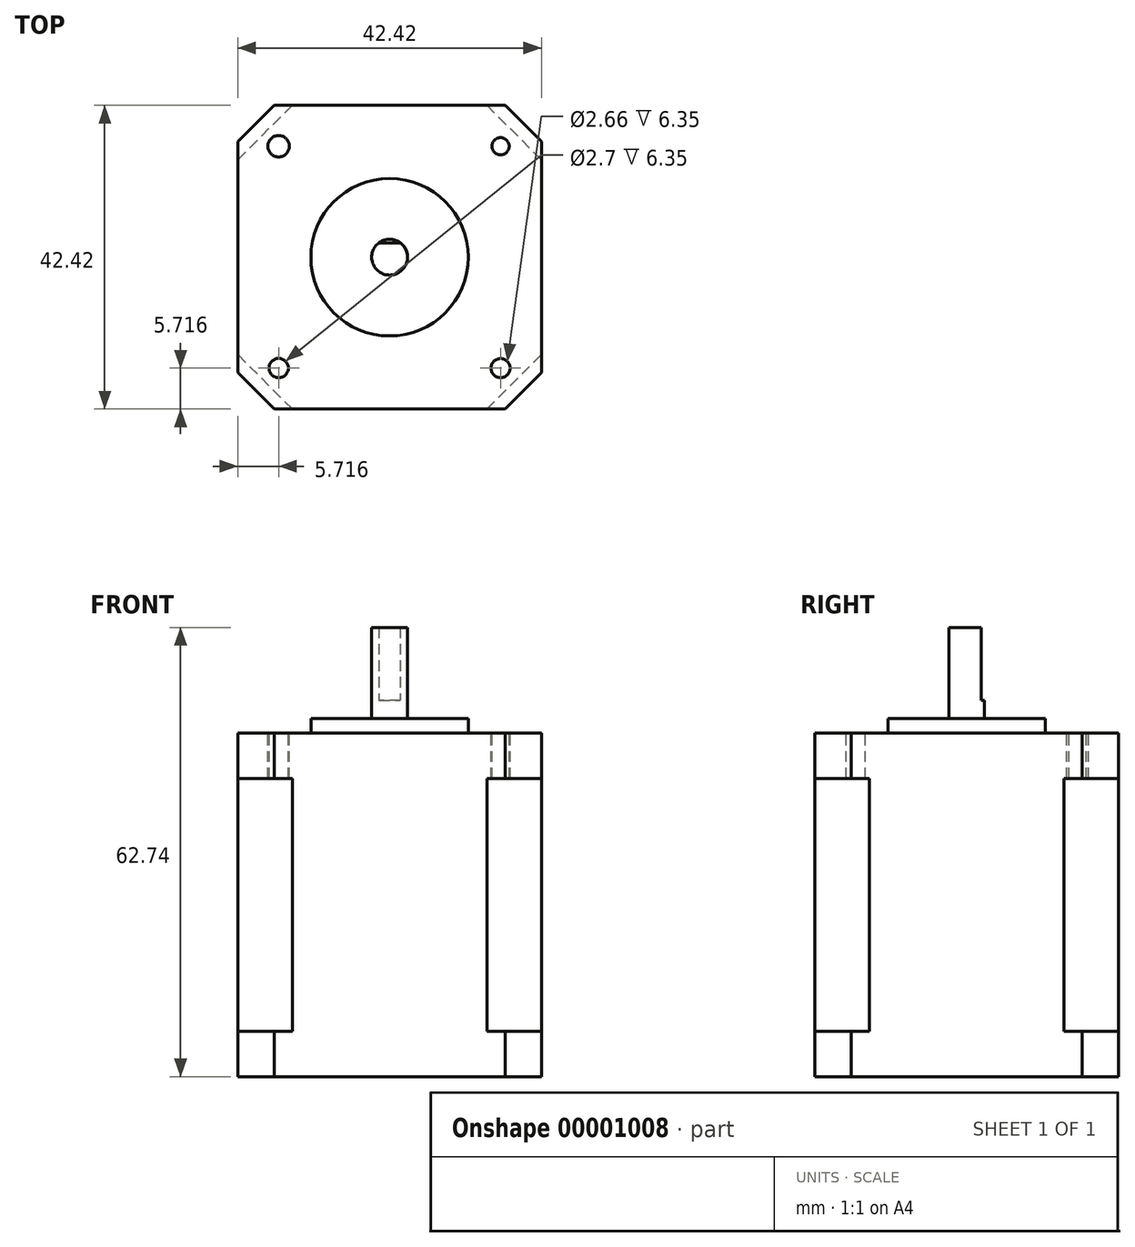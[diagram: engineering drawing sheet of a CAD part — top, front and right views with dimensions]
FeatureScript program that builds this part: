
annotation { "Feature Type Name" : "Feature", "Feature Type Description" : "" }
export const myFeature = defineFeature(function(context is Context, id is Id, definition is map)
    precondition{}
    {
        {
            var Q0;
            Q0=qCreatedBy(makeId("Top.planeOp"),FACE);
            var sketch = newSketch(context, id + "F0", { "sketchPlane" : qUnion([Q0])});
            skLineSegment(sketch, "E0.bottom", {"start": v(-21.2, 21.2) * mm, "end": v(21.2, 21.2) * mm});
            skLineSegment(sketch, "E0.top", {"start": v(-21.2, -21.2) * mm, "end": v(21.2, -21.2) * mm});
            skLineSegment(sketch, "E0.left", {"start": v(-21.2, 21.2) * mm, "end": v(-21.2, -21.2) * mm});
            skLineSegment(sketch, "E0.right", {"start": v(21.2, 21.2) * mm, "end": v(21.2, -21.2) * mm});
            skSolve(sketch);
        }
        {
            var Q0;
            Q0=makeQuery(id+"F0.imprint","IMPRINT",FACE,{"disambiguationData":[TD([[makeQuery(id+"F0.imprint","IMPRINT",EDGE,{"derivedFrom":sQuery(id+"F0.wireOp",EDGE,"E0.bottom")}),-1.0]])]});
            extrude(context, id + "F1", {"entities" : qUnion([Q0]), "endBound" : BoundingType.SYMMETRIC, "depth" : 35.3 * mm});
        }
        {
            var Q0;
            Q0=makeQuery(id+"F1.opExtrude","SWEPT_EDGE",EDGE,{"disambiguationData":[OSD([sQuery(id+"F0.wireOp",EDGE,"E0.bottom"),sQuery(id+"F0.wireOp",EDGE,"E0.right")])]});
            var Q1;
            Q1=makeQuery(id+"F1.opExtrude","SWEPT_EDGE",EDGE,{"disambiguationData":[OSD([sQuery(id+"F0.wireOp",EDGE,"E0.bottom"),sQuery(id+"F0.wireOp",EDGE,"E0.left")])]});
            var Q2;
            Q2=makeQuery(id+"F1.opExtrude","SWEPT_EDGE",EDGE,{"disambiguationData":[OSD([sQuery(id+"F0.wireOp",EDGE,"E0.top"),sQuery(id+"F0.wireOp",EDGE,"E0.left")])]});
            var Q3;
            Q3=makeQuery(id+"F1.opExtrude","SWEPT_EDGE",EDGE,{"disambiguationData":[OSD([sQuery(id+"F0.wireOp",EDGE,"E0.top"),sQuery(id+"F0.wireOp",EDGE,"E0.right")])]});
            chamfer(context, id + "F2", {"entities" : qUnion([Q0, Q1, Q2, Q3]), "width" : 7.62 * mm, "tangentPropagation" : true});
        }
        {
            var Q0;
            Q0=makeQuery(id+"F1.opExtrude","CAP_FACE",FACE,{"disambiguationData":[OSD([sQuery(id+"F0.wireOp",EDGE,"E0.bottom"),sQuery(id+"F0.wireOp",EDGE,"E0.top"),sQuery(id+"F0.wireOp",EDGE,"E0.left"),sQuery(id+"F0.wireOp",EDGE,"E0.right")])],"isStart":false});
            var sketch = newSketch(context, id + "F3", { "sketchPlane" : qUnion([Q0])});
            skLineSegment(sketch, "E1.bottom", {"start": v(-21.2, 21.2) * mm, "end": v(21.2, 21.2) * mm});
            skLineSegment(sketch, "E1.top", {"start": v(-21.2, -21.2) * mm, "end": v(21.2, -21.2) * mm});
            skLineSegment(sketch, "E1.left", {"start": v(-21.2, 21.2) * mm, "end": v(-21.2, -21.2) * mm});
            skLineSegment(sketch, "E1.right", {"start": v(21.2, 21.2) * mm, "end": v(21.2, -21.2) * mm});
            skSolve(sketch);
        }
        {
            var Q0;
            {var subQ0=sQuery(id+"F0.wireOp",EDGE,"E0.top");var subQ1=sQuery(id+"F0.wireOp",EDGE,"E0.right");var subQ2=sQuery(id+"F0.wireOp",EDGE,"E0.bottom");var subQ3=sQuery(id+"F0.wireOp",EDGE,"E0.left");var subQ4=makeQuery(id+"F1.opExtrude","CAP_FACE",FACE,{"disambiguationData":[OSD([subQ2,subQ0,subQ3,subQ1])],"isStart":false});var subQ8=makeQuery(id+"F2.opChamfer","BLEND_EDGE",EDGE,{"blendedFrom":[makeQuery(id+"F1.opExtrude","SWEPT_EDGE",EDGE,{"disambiguationData":[OSD([subQ2,subQ3])]}),subQ4],"blendedInto":[subQ4]});Q0=makeQuery(id+"F3.imprint","IMPRINT",FACE,{"disambiguationData":[TD([[makeQuery(id+"F3.imprint","IMPRINT",EDGE,{"derivedFrom":subQ8}),1.0]])]});}
            var Q1;
            {var subQ0=sQuery(id+"F0.wireOp",EDGE,"E0.bottom");var subQ1=sQuery(id+"F0.wireOp",EDGE,"E0.right");var subQ2=makeQuery(id+"F2.opChamfer","BLEND_EDGE",EDGE,{"blendedFrom":[makeQuery(id+"F1.opExtrude","SWEPT_EDGE",EDGE,{"disambiguationData":[OSD([subQ0,subQ1])]}),makeQuery(id+"F1.opExtrude","CAP_FACE",FACE,{"disambiguationData":[OSD([subQ0,sQuery(id+"F0.wireOp",EDGE,"E0.top"),sQuery(id+"F0.wireOp",EDGE,"E0.left"),subQ1])],"isStart":false})],"blendedInto":[makeQuery(id+"F1.opExtrude","CAP_FACE",FACE,{"disambiguationData":[OSD([subQ0,sQuery(id+"F0.wireOp",EDGE,"E0.top"),sQuery(id+"F0.wireOp",EDGE,"E0.left"),subQ1])],"isStart":false})]});Q1=makeQuery(id+"F3.imprint","IMPRINT",FACE,{"disambiguationData":[TD([[makeQuery(id+"F3.imprint","IMPRINT",EDGE,{"derivedFrom":subQ2}),-1.0]])]});}
            var Q2;
            {var subQ0=sQuery(id+"F0.wireOp",EDGE,"E0.bottom");var subQ1=sQuery(id+"F0.wireOp",EDGE,"E0.left");var subQ2=makeQuery(id+"F2.opChamfer","BLEND_EDGE",EDGE,{"blendedFrom":[makeQuery(id+"F1.opExtrude","SWEPT_EDGE",EDGE,{"disambiguationData":[OSD([subQ0,subQ1])]}),makeQuery(id+"F1.opExtrude","CAP_FACE",FACE,{"disambiguationData":[OSD([subQ0,sQuery(id+"F0.wireOp",EDGE,"E0.top"),subQ1,sQuery(id+"F0.wireOp",EDGE,"E0.right")])],"isStart":false})],"blendedInto":[makeQuery(id+"F1.opExtrude","CAP_FACE",FACE,{"disambiguationData":[OSD([subQ0,sQuery(id+"F0.wireOp",EDGE,"E0.top"),subQ1,sQuery(id+"F0.wireOp",EDGE,"E0.right")])],"isStart":false})]});Q2=makeQuery(id+"F3.imprint","IMPRINT",FACE,{"disambiguationData":[TD([[makeQuery(id+"F3.imprint","IMPRINT",EDGE,{"derivedFrom":subQ2}),-1.0]])]});}
            var Q3;
            {var subQ0=sQuery(id+"F0.wireOp",EDGE,"E0.top");var subQ1=sQuery(id+"F0.wireOp",EDGE,"E0.left");var subQ2=makeQuery(id+"F2.opChamfer","BLEND_EDGE",EDGE,{"blendedFrom":[makeQuery(id+"F1.opExtrude","SWEPT_EDGE",EDGE,{"disambiguationData":[OSD([subQ0,subQ1])]}),makeQuery(id+"F1.opExtrude","CAP_FACE",FACE,{"disambiguationData":[OSD([sQuery(id+"F0.wireOp",EDGE,"E0.bottom"),subQ0,subQ1,sQuery(id+"F0.wireOp",EDGE,"E0.right")])],"isStart":false})],"blendedInto":[makeQuery(id+"F1.opExtrude","CAP_FACE",FACE,{"disambiguationData":[OSD([sQuery(id+"F0.wireOp",EDGE,"E0.bottom"),subQ0,subQ1,sQuery(id+"F0.wireOp",EDGE,"E0.right")])],"isStart":false})]});Q3=makeQuery(id+"F3.imprint","IMPRINT",FACE,{"disambiguationData":[TD([[makeQuery(id+"F3.imprint","IMPRINT",EDGE,{"derivedFrom":subQ2}),-1.0]])]});}
            var Q4;
            {var subQ0=sQuery(id+"F0.wireOp",EDGE,"E0.top");var subQ1=sQuery(id+"F0.wireOp",EDGE,"E0.right");var subQ2=makeQuery(id+"F2.opChamfer","BLEND_EDGE",EDGE,{"blendedFrom":[makeQuery(id+"F1.opExtrude","SWEPT_EDGE",EDGE,{"disambiguationData":[OSD([subQ0,subQ1])]}),makeQuery(id+"F1.opExtrude","CAP_FACE",FACE,{"disambiguationData":[OSD([sQuery(id+"F0.wireOp",EDGE,"E0.bottom"),subQ0,sQuery(id+"F0.wireOp",EDGE,"E0.left"),subQ1])],"isStart":false})],"blendedInto":[makeQuery(id+"F1.opExtrude","CAP_FACE",FACE,{"disambiguationData":[OSD([sQuery(id+"F0.wireOp",EDGE,"E0.bottom"),subQ0,sQuery(id+"F0.wireOp",EDGE,"E0.left"),subQ1])],"isStart":false})]});Q4=makeQuery(id+"F3.imprint","IMPRINT",FACE,{"disambiguationData":[TD([[makeQuery(id+"F3.imprint","IMPRINT",EDGE,{"derivedFrom":subQ2}),-1.0]])]});}
            extrude(context, id + "F4", {"entities" : qUnion([Q0, Q1, Q2, Q3, Q4]), "operationType" : NewBodyOperationType.ADD, "depth" : 6.35 * mm});
        }
        {
            var Q0;
            Q0=makeQuery(id+"F4.opExtrude","SWEPT_EDGE",EDGE,{"disambiguationData":[OSD([sQuery(id+"F3.wireOp",EDGE,"E1.bottom"),sQuery(id+"F3.wireOp",EDGE,"E1.right")])]});
            var Q1;
            Q1=makeQuery(id+"F4.opExtrude","SWEPT_EDGE",EDGE,{"disambiguationData":[OSD([sQuery(id+"F3.wireOp",EDGE,"E1.bottom"),sQuery(id+"F3.wireOp",EDGE,"E1.left")])]});
            var Q2;
            Q2=makeQuery(id+"F4.opExtrude","SWEPT_EDGE",EDGE,{"disambiguationData":[OSD([sQuery(id+"F3.wireOp",EDGE,"E1.top"),sQuery(id+"F3.wireOp",EDGE,"E1.left")])]});
            var Q3;
            Q3=makeQuery(id+"F4.opExtrude","SWEPT_EDGE",EDGE,{"disambiguationData":[OSD([sQuery(id+"F3.wireOp",EDGE,"E1.top"),sQuery(id+"F3.wireOp",EDGE,"E1.right")])]});
            chamfer(context, id + "F5", {"entities" : qUnion([Q0, Q1, Q2, Q3]), "width" : 5.08 * mm, "tangentPropagation" : true});
        }
        {
            var Q0;
            Q0=makeQuery(id+"F1.opExtrude","CAP_FACE",FACE,{"disambiguationData":[OSD([sQuery(id+"F0.wireOp",EDGE,"E0.bottom"),sQuery(id+"F0.wireOp",EDGE,"E0.top"),sQuery(id+"F0.wireOp",EDGE,"E0.left"),sQuery(id+"F0.wireOp",EDGE,"E0.right")])],"isStart":true});
            var sketch = newSketch(context, id + "F6", { "sketchPlane" : qUnion([Q0])});
            skLineSegment(sketch, "E2.0.0", {"start": v(-16.13, 21.2) * mm, "end": v(16.13, 21.2) * mm});
            skLineSegment(sketch, "E2.0.1", {"start": v(16.13, 21.2) * mm, "end": v(21.2, 16.13) * mm});
            skLineSegment(sketch, "E2.0.2", {"start": v(21.2, -16.13) * mm, "end": v(21.2, 16.13) * mm});
            skLineSegment(sketch, "E2.0.3", {"start": v(21.2, -16.13) * mm, "end": v(16.13, -21.2) * mm});
            skLineSegment(sketch, "E2.0.4", {"start": v(-16.13, -21.2) * mm, "end": v(16.13, -21.2) * mm});
            skLineSegment(sketch, "E2.0.5", {"start": v(-16.13, -21.2) * mm, "end": v(-21.2, -16.13) * mm});
            skLineSegment(sketch, "E2.0.6", {"start": v(-21.2, -16.13) * mm, "end": v(-21.2, 16.13) * mm});
            skLineSegment(sketch, "E2.0.7", {"start": v(-21.2, 16.13) * mm, "end": v(-16.13, 21.2) * mm});
            skSolve(sketch);
        }
        {
            var Q0;
            {var subQ3=sQuery(id+"F6.wireOp",EDGE,"E2.0.7");Q0=makeQuery(id+"F6.imprint","IMPRINT",FACE,{"disambiguationData":[TD([[makeQuery(id+"F6.imprint","IMPRINT",EDGE,{"derivedFrom":subQ3}),-1.0]])]});}
            var Q1;
            {var subQ4=sQuery(id+"F6.wireOp",EDGE,"E2.0.1");Q1=makeQuery(id+"F6.imprint","IMPRINT",FACE,{"disambiguationData":[TD([[makeQuery(id+"F6.imprint","IMPRINT",EDGE,{"derivedFrom":subQ4}),-1.0]])]});}
            var Q2;
            {var subQ4=sQuery(id+"F6.wireOp",EDGE,"E2.0.3");Q2=makeQuery(id+"F6.imprint","IMPRINT",FACE,{"disambiguationData":[TD([[makeQuery(id+"F6.imprint","IMPRINT",EDGE,{"derivedFrom":subQ4}),-1.0]])]});}
            var Q3;
            {var subQ4=sQuery(id+"F6.wireOp",EDGE,"E2.0.5");Q3=makeQuery(id+"F6.imprint","IMPRINT",FACE,{"disambiguationData":[TD([[makeQuery(id+"F6.imprint","IMPRINT",EDGE,{"derivedFrom":subQ4}),-1.0]])]});}
            var Q4;
            {var subQ0=sQuery(id+"F0.wireOp",EDGE,"E0.top");var subQ1=sQuery(id+"F0.wireOp",EDGE,"E0.right");var subQ2=sQuery(id+"F0.wireOp",EDGE,"E0.bottom");var subQ3=sQuery(id+"F0.wireOp",EDGE,"E0.left");var subQ4=makeQuery(id+"F1.opExtrude","CAP_FACE",FACE,{"disambiguationData":[OSD([subQ2,subQ0,subQ3,subQ1])],"isStart":true});var subQ8=makeQuery(id+"F2.opChamfer","BLEND_EDGE",EDGE,{"blendedFrom":[makeQuery(id+"F1.opExtrude","SWEPT_EDGE",EDGE,{"disambiguationData":[OSD([subQ2,subQ3])]}),subQ4],"blendedInto":[subQ4]});Q4=makeQuery(id+"F6.imprint","IMPRINT",FACE,{"disambiguationData":[TD([[makeQuery(id+"F6.imprint","IMPRINT",EDGE,{"derivedFrom":subQ8}),1.0]])]});}
            extrude(context, id + "F7", {"entities" : qUnion([Q0, Q1, Q2, Q3, Q4]), "operationType" : NewBodyOperationType.ADD, "depth" : 6.35 * mm});
        }
        {
            var Q0;
            Q0=makeQuery(id+"F4.opExtrude","CAP_FACE",FACE,{"disambiguationData":[OSD([sQuery(id+"F3.wireOp",EDGE,"E1.bottom"),sQuery(id+"F3.wireOp",EDGE,"E1.top"),sQuery(id+"F3.wireOp",EDGE,"E1.left"),sQuery(id+"F3.wireOp",EDGE,"E1.right")])],"isStart":false});
            var sketch = newSketch(context, id + "F8", { "sketchPlane" : qUnion([Q0])});
            skCircle(sketch, "E3", {"center": v(0, 0) * mm, "radius": 11 * mm});
            skSolve(sketch);
        }
        {
            var Q0;
            Q0=makeQuery(id+"F8.imprint","IMPRINT",FACE,{"disambiguationData":[TD([[makeQuery(id+"F8.imprint","IMPRINT",EDGE,{"derivedFrom":sQuery(id+"F8.wireOp",EDGE,"E3")}),1.0]])]});
            extrude(context, id + "F9", {"entities" : qUnion([Q0]), "operationType" : NewBodyOperationType.ADD, "depth" : 2.03 * mm});
        }
        {
            var Q0;
            Q0=makeQuery(id+"F9.opExtrude","CAP_FACE",FACE,{"disambiguationData":[OSD([sQuery(id+"F8.wireOp",EDGE,"E3")])],"isStart":false});
            var sketch = newSketch(context, id + "F10", { "sketchPlane" : qUnion([Q0])});
            skCircle(sketch, "E4", {"center": v(0, 0) * mm, "radius": 2.5 * mm});
            skSolve(sketch);
        }
        {
            var Q0;
            Q0=makeQuery(id+"F10.imprint","IMPRINT",FACE,{"disambiguationData":[TD([[makeQuery(id+"F10.imprint","IMPRINT",EDGE,{"derivedFrom":sQuery(id+"F10.wireOp",EDGE,"E4")}),1.0]])]});
            extrude(context, id + "F11", {"entities" : qUnion([Q0]), "operationType" : NewBodyOperationType.ADD, "depth" : 12.7 * mm});
        }
        {
            var Q0;
            Q0=makeQuery(id+"F11.opExtrude","CAP_FACE",FACE,{"disambiguationData":[OSD([sQuery(id+"F10.wireOp",EDGE,"E4")])],"isStart":false});
            var sketch = newSketch(context, id + "F12", { "sketchPlane" : qUnion([Q0])});
            skLineSegment(sketch, "E5.bottom", {"start": v(-2.63, 2.93) * mm, "end": v(2.62, 2.93) * mm});
            skLineSegment(sketch, "E5.top", {"start": v(-2.63, 2) * mm, "end": v(2.62, 2) * mm});
            skLineSegment(sketch, "E5.left", {"start": v(-2.63, 2.93) * mm, "end": v(-2.63, 2) * mm});
            skLineSegment(sketch, "E5.right", {"start": v(2.62, 2.93) * mm, "end": v(2.62, 2) * mm});
            skSolve(sketch);
        }
        {
            var Q0;
            {var subQ0=makeQuery(id+"F11.opExtrude","CAP_EDGE",EDGE,{"disambiguationData":[OSD([sQuery(id+"F10.wireOp",EDGE,"E4")])],"isStart":false});var subQ1=sQuery(id+"F12.wireOp",EDGE,"E5.top");var subQ3=makeQuery(id+"F12.imprint","INTERSECT",VERTEX,{"disambiguationData":[OD(0.0)],"derivedFrom":[subQ0,subQ1]});Q0=qUnion([makeQuery(id+"F12.imprint","IMPRINT",FACE,{"disambiguationData":[TD([[makeQuery(id+"F12.imprint","IMPRINT",EDGE,{"derivedFrom":sQuery(id+"F12.wireOp",EDGE,"E5.bottom")}),-1.0]])]}),makeQuery(id+"F12.imprint","IMPRINT",FACE,{"disambiguationData":[TD([[makeQuery(id+"F12.imprint","IMPRINT",EDGE,{"disambiguationData":[TD([[subQ3,-1.0]])],"derivedFrom":subQ1}),1.0]])]})]);}
            extrude(context, id + "F13", {"entities" : qUnion([Q0]), "operationType" : NewBodyOperationType.REMOVE, "oppositeDirection" : true, "depth" : 10.16 * mm});
        }
        {
            var Q0;
            Q0=makeQuery(id+"F4.opExtrude","CAP_FACE",FACE,{"disambiguationData":[OSD([sQuery(id+"F3.wireOp",EDGE,"E1.bottom"),sQuery(id+"F3.wireOp",EDGE,"E1.top"),sQuery(id+"F3.wireOp",EDGE,"E1.left"),sQuery(id+"F3.wireOp",EDGE,"E1.right")])],"isStart":false});
            var sketch = newSketch(context, id + "F14", { "sketchPlane" : qUnion([Q0])});
            skCircle(sketch, "E6", {"center": v(-15.5, 15.5) * mm, "radius": 1.5 * mm});
            skCircle(sketch, "E7", {"center": v(15.5, 15.5) * mm, "radius": 1.2 * mm});
            skCircle(sketch, "E8", {"center": v(15.5, -15.5) * mm, "radius": 1.33 * mm});
            skCircle(sketch, "E9", {"center": v(-15.5, -15.5) * mm, "radius": 1.35 * mm});
            skSolve(sketch);
        }
        {
            var Q0;
            {Q0=qUnion([makeQuery(id+"F14.imprint","IMPRINT",FACE,{"disambiguationData":[TD([[makeQuery(id+"F14.imprint","IMPRINT",EDGE,{"derivedFrom":sQuery(id+"F14.wireOp",EDGE,"E6")}),1.0]])]}),makeQuery(id+"F14.imprint","IMPRINT",FACE,{"disambiguationData":[TD([[makeQuery(id+"F14.imprint","IMPRINT",EDGE,{"derivedFrom":sQuery(id+"F14.wireOp",EDGE,"E7")}),1.0]])]}),makeQuery(id+"F14.imprint","IMPRINT",FACE,{"disambiguationData":[TD([[makeQuery(id+"F14.imprint","IMPRINT",EDGE,{"derivedFrom":sQuery(id+"F14.wireOp",EDGE,"E8")}),1.0]])]}),makeQuery(id+"F14.imprint","IMPRINT",FACE,{"disambiguationData":[TD([[makeQuery(id+"F14.imprint","IMPRINT",EDGE,{"derivedFrom":sQuery(id+"F14.wireOp",EDGE,"E9")}),1.0]])]})]);}
            extrude(context, id + "F15", {"entities" : qUnion([Q0]), "operationType" : NewBodyOperationType.REMOVE, "oppositeDirection" : true, "depth" : 6.35 * mm});
        }
    });
